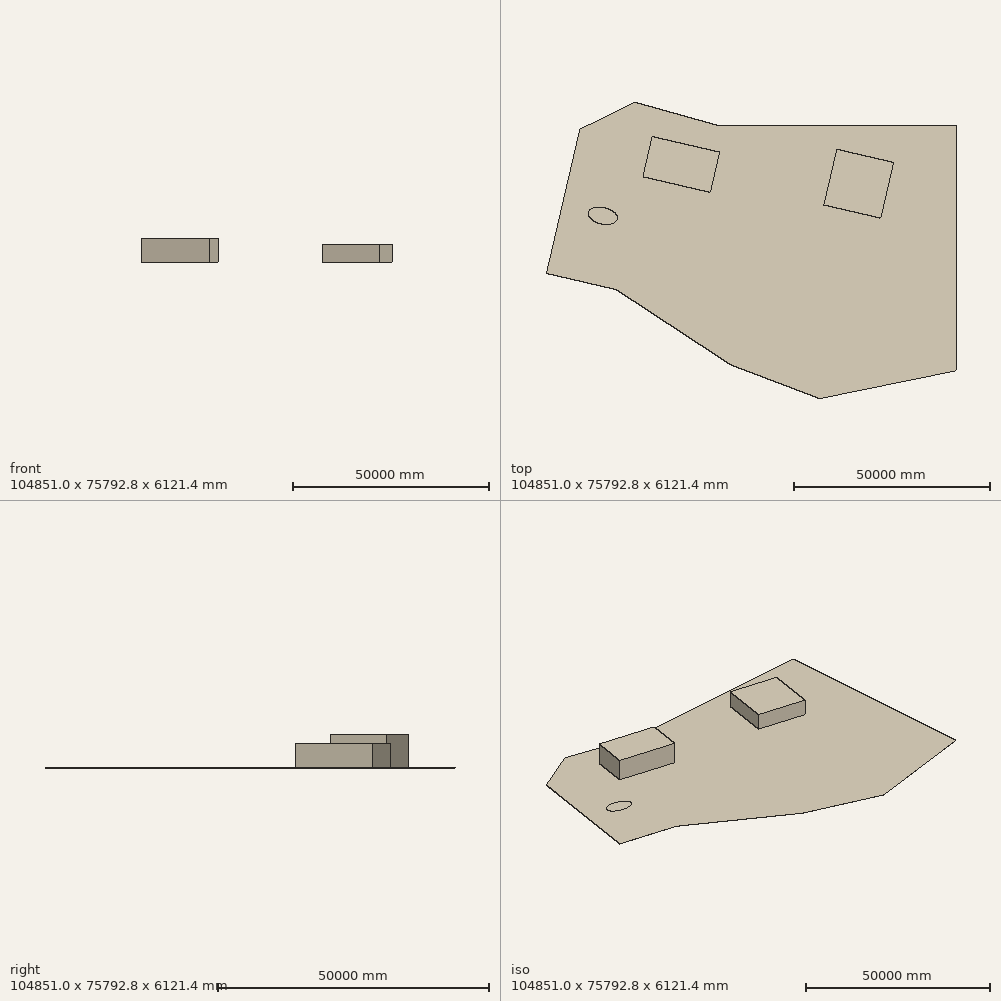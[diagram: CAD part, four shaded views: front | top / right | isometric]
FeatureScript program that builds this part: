
annotation { "Feature Type Name" : "Feature", "Feature Type Description" : "" }
export const myFeature = defineFeature(function(context is Context, id is Id, definition is map)
    precondition{}
    {
        {
            var Q0;
            Q0=qCreatedBy(makeId("Top.planeOp"),FACE);
            var sketch = newSketch(context, id + "F0", { "sketchPlane" : qUnion([Q0])});
            skLineSegment(sketch, "E0", {"start": v(0, 0) * mm, "end": v(-34941.26, -7131.46) * mm});
            skLineSegment(sketch, "E1", {"start": v(-34941.26, -7131.46) * mm, "end": v(-57738.57, 1520.83) * mm});
            skLineSegment(sketch, "E2", {"start": v(-57738.57, 1520.83) * mm, "end": v(-87035.3, 20765.18) * mm});
            skLineSegment(sketch, "E3", {"start": v(-87035.3, 20765.18) * mm, "end": v(-104850.97, 24894.63) * mm});
            skLineSegment(sketch, "E4", {"start": v(-104850.97, 24894.63) * mm, "end": v(-96316.77, 61713.71) * mm});
            skLineSegment(sketch, "E5", {"start": v(-96316.77, 61713.71) * mm, "end": v(-82155.86, 68661.29) * mm});
            skLineSegment(sketch, "E6", {"start": v(-82155.86, 68661.29) * mm, "end": v(-60961.69, 62737.12) * mm});
            skLineSegment(sketch, "E7", {"start": v(-60961.69, 62737.12) * mm, "end": v(-1.69, 62737.12) * mm});
            skLineSegment(sketch, "E8", {"start": v(-1.69, 62737.12) * mm, "end": v(-1.69, 9.28) * mm});
            skLineSegment(sketch, "E9", {"start": v(-1.69, 9.28) * mm, "end": v(0, 0) * mm});
            skLineSegment(sketch, "E10.bottom", {"start": v(-77805.32, 59911.05) * mm, "end": v(-60534, 55907.78) * mm});
            skLineSegment(sketch, "E10.top", {"start": v(-80191.23, 49617.55) * mm, "end": v(-62919.92, 45614.27) * mm});
            skLineSegment(sketch, "E10.left", {"start": v(-77805.32, 59911.05) * mm, "end": v(-80191.23, 49617.55) * mm});
            skLineSegment(sketch, "E10.right", {"start": v(-60534, 55907.78) * mm, "end": v(-62919.92, 45614.27) * mm});
            skLineSegment(sketch, "E11", {"start": v(-80191.23, 49617.55) * mm, "end": v(-98155.38, 53781.41) * mm, "construction": true});
            skLineSegment(sketch, "E12.bottom", {"start": v(-30585.28, 56650.1) * mm, "end": v(-16035.8, 53277.71) * mm});
            skLineSegment(sketch, "E12.top", {"start": v(-33888.84, 42397.55) * mm, "end": v(-19339.37, 39025.16) * mm});
            skLineSegment(sketch, "E12.left", {"start": v(-30585.28, 56650.1) * mm, "end": v(-33888.84, 42397.55) * mm});
            skLineSegment(sketch, "E12.right", {"start": v(-16035.8, 53277.71) * mm, "end": v(-19339.37, 39025.16) * mm});
            skLineSegment(sketch, "E13", {"start": v(-56902.14, 3159.47) * mm, "end": v(-86304.2, 22473) * mm});
            skLineSegment(sketch, "E14", {"start": v(-86304.2, 22473) * mm, "end": v(-104438.03, 26676.2) * mm});
            skLineSegment(sketch, "E15", {"start": v(-56902.14, 3159.47) * mm, "end": v(-36770.06, -4481.3) * mm});
            skLineSegment(sketch, "E16", {"start": v(-1.69, 3110.5) * mm, "end": v(-33112.46, -3647.37) * mm});
            skLineSegment(sketch, "E17", {"start": v(-33112.46, -3647.37) * mm, "end": v(-33112.46, -599.37) * mm});
            skLineSegment(sketch, "E18", {"start": v(-33112.46, -599.37) * mm, "end": v(-36770.06, -599.37) * mm});
            skLineSegment(sketch, "E19", {"start": v(-36770.06, -599.37) * mm, "end": v(-36770.06, -4481.3) * mm});
            skLineSegment(sketch, "E20", {"start": v(-36770.06, -599.37) * mm, "end": v(-52808.58, 24293.57) * mm});
            skLineSegment(sketch, "E21", {"start": v(-52808.58, 24293.57) * mm, "end": v(-71669.8, 28615.8) * mm});
            skLineSegment(sketch, "E22", {"start": v(-71669.8, 28615.8) * mm, "end": v(-69751.01, 32034.75) * mm});
            skLineSegment(sketch, "E23", {"start": v(-69751.01, 32034.75) * mm, "end": v(-54855.5, 33926.56) * mm});
            skLineSegment(sketch, "E24", {"start": v(-54855.5, 33926.56) * mm, "end": v(-55777.03, 41182.3) * mm});
            skLineSegment(sketch, "E25", {"start": v(-55777.03, 41182.3) * mm, "end": v(-62699.36, 44806.92) * mm});
            skLineSegment(sketch, "E26", {"start": v(-33112.46, -599.37) * mm, "end": v(-47275.12, 23302.32) * mm});
            skLineSegment(sketch, "E27", {"start": v(-47275.12, 23302.32) * mm, "end": v(-45391.38, 37276.55) * mm});
            skLineSegment(sketch, "E28", {"start": v(-45391.38, 37276.55) * mm, "end": v(-35954.78, 45371.33) * mm});
            skLineSegment(sketch, "E29", {"start": v(-56674.76, 49471.68) * mm, "end": v(-49770.19, 46958.86) * mm});
            skLineSegment(sketch, "E30", {"start": v(-49770.19, 46958.86) * mm, "end": v(-38038.24, 56785.51) * mm});
            skLineSegment(sketch, "E31", {"start": v(-30585.28, 56650.1) * mm, "end": v(-29174.38, 62737.12) * mm, "construction": true});
            skLineSegment(sketch, "E32", {"start": v(-16035.8, 53277.71) * mm, "end": v(-1.69, 49561.2) * mm, "construction": true});
            skLineSegment(sketch, "E33", {"start": v(-60534, 55907.78) * mm, "end": v(-58951.05, 62737.12) * mm, "construction": true});
            skEllipse(sketch, "E34", {"center": v(-90416.86, 39628.94) * mm, "majorRadius": 3810 * mm, "minorRadius": 2133.6 * mm, "majorAxis": v(-0.97, 0.23)});
            skLineSegment(sketch, "E35", {"start": v(-89935.1, 41707.43) * mm, "end": v(-90898.63, 37550.44) * mm, "construction": true});
            skSolve(sketch);
        }
        {
            var Q0;
            Q0=makeQuery(id+"F0.imprint","IMPRINT",FACE,{"disambiguationData":[TD([[makeQuery(id+"F0.imprint","IMPRINT",EDGE,{"derivedFrom":sQuery(id+"F0.wireOp",EDGE,"E0")}),-1.0]])]});
            var Q1;
            Q1=makeQuery(id+"F0.imprint","IMPRINT",FACE,{"disambiguationData":[TD([[makeQuery(id+"F0.imprint","IMPRINT",EDGE,{"derivedFrom":sQuery(id+"F0.wireOp",EDGE,"E12.bottom")}),-1.0]])]});
            var Q2;
            Q2=makeQuery(id+"F0.imprint","IMPRINT",FACE,{"disambiguationData":[TD([[makeQuery(id+"F0.imprint","IMPRINT",EDGE,{"derivedFrom":sQuery(id+"F0.wireOp",EDGE,"E10.bottom")}),-1.0]])]});
            var Q3;
            Q3=makeQuery(id+"F0.imprint","IMPRINT",FACE,{"disambiguationData":[TD([[makeQuery(id+"F0.imprint","IMPRINT",EDGE,{"derivedFrom":sQuery(id+"F0.wireOp",EDGE,"UWOaQsLA-SRak-WEsL-T55y-4dl8ampZTXso")}),1.0]])]});
            var Q4;
            {var subQ4=sQuery(id+"F0.wireOp",EDGE,"E5");Q4=makeQuery(id+"F0.imprint","IMPRINT",FACE,{"disambiguationData":[TD([[makeQuery(id+"F0.imprint","IMPRINT",EDGE,{"derivedFrom":subQ4}),-1.0]])]});}
            extrude(context, id + "F1", {"entities" : qUnion([Q0, Q1, Q2, Q3, Q4]), "oppositeDirection" : true, "depth" : 25.4 * mm});
        }
        {
            var Q0;
            Q0=makeQuery(id+"F0.imprint","IMPRINT",FACE,{"disambiguationData":[TD([[makeQuery(id+"F0.imprint","IMPRINT",EDGE,{"derivedFrom":sQuery(id+"F0.wireOp",EDGE,"E10.bottom")}),-1.0]])]});
            extrude(context, id + "F2", {"entities" : qUnion([Q0]), "depth" : 6096 * mm});
        }
        {
            var Q0;
            Q0=makeQuery(id+"F0.imprint","IMPRINT",FACE,{"disambiguationData":[TD([[makeQuery(id+"F0.imprint","IMPRINT",EDGE,{"derivedFrom":sQuery(id+"F0.wireOp",EDGE,"E12.bottom")}),-1.0]])]});
            extrude(context, id + "F3", {"entities" : qUnion([Q0]), "depth" : 4572 * mm});
        }
        {
            var Q0;
            Q0=makeQuery(id+"F0.imprint","IMPRINT",FACE,{"disambiguationData":[TD([[makeQuery(id+"F0.imprint","IMPRINT",EDGE,{"derivedFrom":sQuery(id+"F0.wireOp",EDGE,"E34")}),1.0]])]});
            var Q1;
            Q1=sQuery(id+"F0.wireOp",EDGE,"UWOaQsLA-SRak-WEsL-T55y-4dl8ampZTXso");
            var Q2;
            Q2=makeQuery(id+"F1.opExtrude","CAP_FACE",FACE,{"disambiguationData":[OSD([sQuery(id+"F0.wireOp",EDGE,"E0"),sQuery(id+"F0.wireOp",EDGE,"E1"),sQuery(id+"F0.wireOp",EDGE,"E2"),sQuery(id+"F0.wireOp",EDGE,"E3"),sQuery(id+"F0.wireOp",EDGE,"E4"),sQuery(id+"F0.wireOp",EDGE,"E5"),sQuery(id+"F0.wireOp",EDGE,"E6"),sQuery(id+"F0.wireOp",EDGE,"E7"),sQuery(id+"F0.wireOp",EDGE,"E8"),sQuery(id+"F0.wireOp",EDGE,"E9"),sQuery(id+"F0.wireOp",EDGE,"E34")])],"isStart":false});
            extrude(context, id + "F4", {"entities" : qUnion([Q0]), "operationType" : NewBodyOperationType.REMOVE, "surfaceEntities" : qUnion([Q1]), "endBound" : BoundingType.UP_TO_SURFACE, "oppositeDirection" : true, "endBoundEntityFace" : qUnion([Q2]), "depth" : 25.4 * mm});
        }
        {
            var Q0;
            Q0=makeQuery(id+"F0.imprint","IMPRINT",FACE,{"disambiguationData":[TD([[makeQuery(id+"F0.imprint","IMPRINT",EDGE,{"derivedFrom":sQuery(id+"F0.wireOp",EDGE,"E34")}),1.0]])]});
            var Q1;
            Q1=makeQuery(id+"F1.opExtrude","CAP_FACE",FACE,{"disambiguationData":[OSD([sQuery(id+"F0.wireOp",EDGE,"E0"),sQuery(id+"F0.wireOp",EDGE,"E1"),sQuery(id+"F0.wireOp",EDGE,"E2"),sQuery(id+"F0.wireOp",EDGE,"E3"),sQuery(id+"F0.wireOp",EDGE,"E4"),sQuery(id+"F0.wireOp",EDGE,"E5"),sQuery(id+"F0.wireOp",EDGE,"E6"),sQuery(id+"F0.wireOp",EDGE,"E7"),sQuery(id+"F0.wireOp",EDGE,"E8"),sQuery(id+"F0.wireOp",EDGE,"E9")])],"isStart":false});
            extrude(context, id + "F5", {"entities" : qUnion([Q0]), "endBound" : BoundingType.UP_TO_SURFACE, "oppositeDirection" : true, "endBoundEntityFace" : qUnion([Q1]), "depth" : 25.4 * mm});
        }
    });
